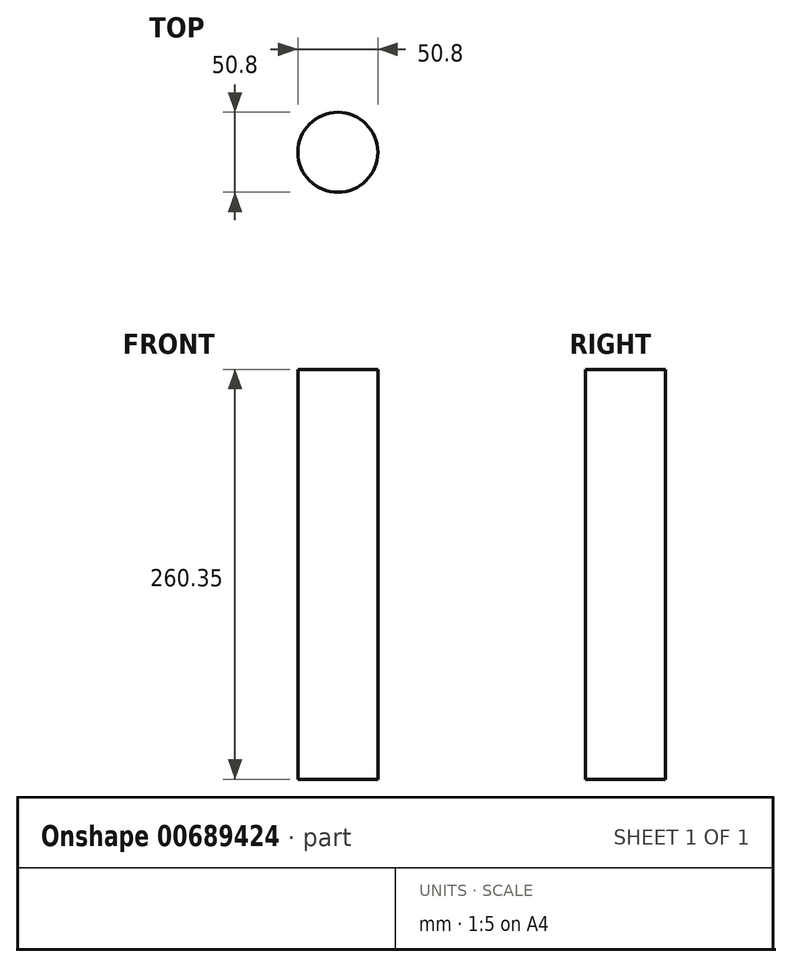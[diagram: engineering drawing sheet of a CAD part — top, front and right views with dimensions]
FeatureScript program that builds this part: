
annotation { "Feature Type Name" : "Feature", "Feature Type Description" : "" }
export const myFeature = defineFeature(function(context is Context, id is Id, definition is map)
    precondition{}
    {
        {
            var Q0;
            Q0=qCreatedBy(makeId("Top.planeOp"),FACE);
            var sketch = newSketch(context, id + "F0", { "sketchPlane" : qUnion([Q0])});
            skCircle(sketch, "E0", {"center": v(0, 0) * mm, "radius": 25.4 * mm});
            skSolve(sketch);
        }
        {
            var Q0;
            Q0=makeQuery(id+"F0.imprint","IMPRINT",FACE,{"disambiguationData":[TD([[makeQuery(id+"F0.imprint","IMPRINT",EDGE,{"derivedFrom":sQuery(id+"F0.wireOp",EDGE,"E0")}),1.0]])]});
            extrude(context, id + "F1", {"entities" : qUnion([Q0]), "depth" : 260.35 * mm, "offsetDistance" : 25.4 * mm});
        }
    });
